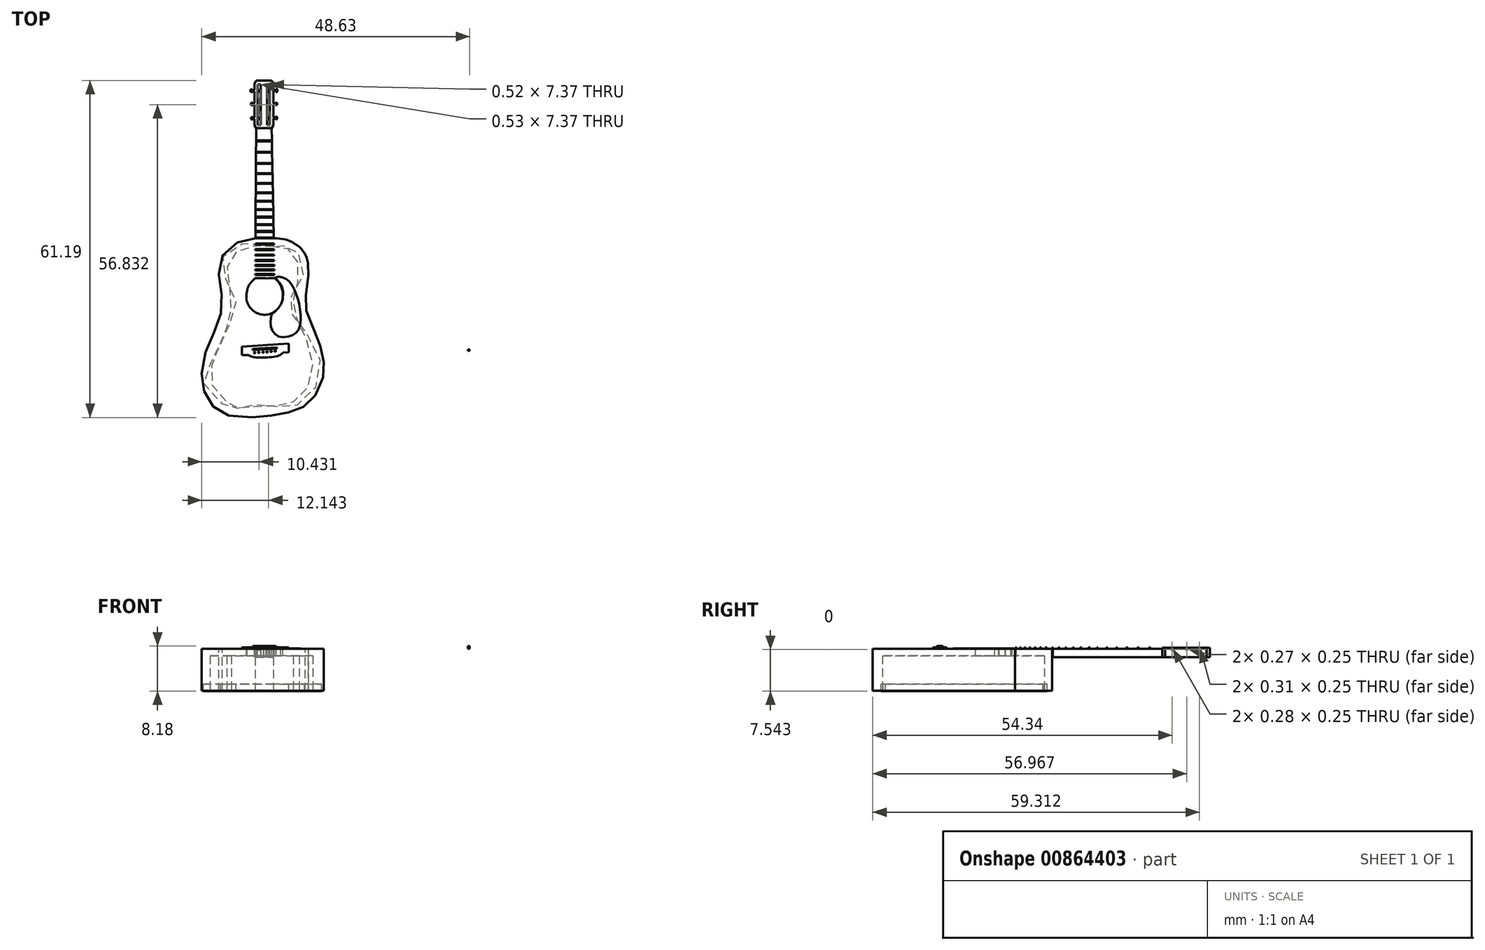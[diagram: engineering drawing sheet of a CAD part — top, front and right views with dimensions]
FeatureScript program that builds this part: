
annotation { "Feature Type Name" : "Feature", "Feature Type Description" : "" }
export const myFeature = defineFeature(function(context is Context, id is Id, definition is map)
    precondition{}
    {
        {
            var Q0;
            Q0=qCreatedBy(makeId("Top.planeOp"),FACE);
            var sketch = newSketch(context, id + "F0", { "sketchPlane" : qUnion([Q0])});
            skFitSpline(sketch, "E0", {"points": [v(22.3, 27.84) * mm, v(21.98, 25.02) * mm, v(21.82, 23.2) * mm, v(21.9, 21.62) * mm, v(22.91, 18.86) * mm, v(23.74, 17) * mm, v(24.5, 15.03) * mm, v(24.98, 13.15) * mm, v(25.13, 11.5) * mm, v(25.05, 9.87) * mm, v(24.78, 8.47) * mm, v(23.46, 5.83) * mm, v(22.27, 4.58) * mm, v(20.8, 3.57) * mm, v(19.22, 3.03) * mm, v(17.28, 2.58) * mm, v(15.34, 2.32) * mm, v(13.15, 2.13) * mm, v(9, 2.1) * mm, v(6.86, 2.83) * mm, v(5.05, 4) * mm, v(3.85, 5.8) * mm, v(3.1, 7.79) * mm, v(2.99, 9.87) * mm, v(3.35, 12.84) * mm, v(4.55, 16.01) * mm, v(5.6, 18.36) * mm, v(6.5, 21.1) * mm, v(6.69, 23.35) * mm, v(6.24, 26.4) * mm, v(6.08, 28.64) * mm, v(6.58, 31.1) * mm, v(8.32, 33.03) * mm, v(10.45, 34.2) * mm, v(12.74, 34.53) * mm], "startDerivative": vector(-10.71, -89.78) * mm, "endDerivative": vector(78.7, 5.6) * mm});
            skLineSegment(sketch, "E1", {"start": v(16.21, 27.29) * mm, "end": v(15.66, 54.52) * mm});
            skLineSegment(sketch, "E2", {"start": v(15.66, 54.52) * mm, "end": v(12.87, 54.52) * mm});
            skLineSegment(sketch, "E3", {"start": v(12.87, 54.52) * mm, "end": v(12.67, 27.29) * mm});
            skLineSegment(sketch, "E4", {"start": v(12.67, 27.29) * mm, "end": v(16.21, 27.29) * mm});
            skLineSegment(sketch, "E5", {"start": v(12.86, 52.31) * mm, "end": v(15.7, 52.37) * mm});
            skLineSegment(sketch, "E6", {"start": v(12.84, 50.24) * mm, "end": v(15.75, 50.3) * mm});
            skLineSegment(sketch, "E7", {"start": v(12.83, 48.25) * mm, "end": v(15.79, 48.22) * mm});
            skLineSegment(sketch, "E8", {"start": v(12.81, 46.37) * mm, "end": v(15.83, 46.35) * mm});
            skLineSegment(sketch, "E9", {"start": v(12.8, 44.6) * mm, "end": v(15.86, 44.58) * mm});
            skLineSegment(sketch, "E10", {"start": v(12.79, 42.9) * mm, "end": v(15.9, 42.87) * mm});
            skLineSegment(sketch, "E11", {"start": v(12.78, 41.39) * mm, "end": v(15.93, 41.36) * mm});
            skLineSegment(sketch, "E12", {"start": v(12.77, 39.85) * mm, "end": v(15.96, 39.83) * mm});
            skPoint(sketch, "E13.end.orphan", {"position": v(15.96, 38.48) * mm});
            skLineSegment(sketch, "E14", {"start": v(12.76, 38.46) * mm, "end": v(15.99, 38.46) * mm});
            skLineSegment(sketch, "E15", {"start": v(12.75, 37.12) * mm, "end": v(16.01, 37.12) * mm});
            skLineSegment(sketch, "E16", {"start": v(12.74, 35.86) * mm, "end": v(16.04, 35.86) * mm});
            skLineSegment(sketch, "E17", {"start": v(12.73, 34.67) * mm, "end": v(16.06, 34.67) * mm});
            skLineSegment(sketch, "E18", {"start": v(12.72, 33.58) * mm, "end": v(16.09, 33.58) * mm});
            skLineSegment(sketch, "E19", {"start": v(12.71, 32.56) * mm, "end": v(16.1, 32.56) * mm});
            skLineSegment(sketch, "E20", {"start": v(12.7, 31.58) * mm, "end": v(16.13, 31.58) * mm});
            skLineSegment(sketch, "E21", {"start": v(12.7, 30.6) * mm, "end": v(16.15, 30.6) * mm});
            skLineSegment(sketch, "E22", {"start": v(12.7, 29.73) * mm, "end": v(16.16, 29.73) * mm});
            skLineSegment(sketch, "E23", {"start": v(12.69, 28.89) * mm, "end": v(16.18, 28.89) * mm});
            skLineSegment(sketch, "E24", {"start": v(12.68, 28.04) * mm, "end": v(16.2, 28.04) * mm});
            skLineSegment(sketch, "E25", {"start": v(16.2, 28.04) * mm, "end": v(16.2, 28.06) * mm});
            skPoint(sketch, "E26.2.internal.orphan", {"position": v(15.85, 25.8) * mm});
            skPoint(sketch, "E27.0.internal.orphan", {"position": v(16.2, 34.53) * mm});
            skFitSpline(sketch, "E28", {"points": [v(22.3, 27.84) * mm, v(22.3, 28.93) * mm, v(22.2, 30.45) * mm, v(21.61, 31.9) * mm, v(20.8, 32.88) * mm, v(19.34, 33.86) * mm, v(17.95, 34.37) * mm, v(16.52, 34.55) * mm, v(16.07, 34.53) * mm], "startDerivative": vector(0, 9.07) * mm, "endDerivative": vector(-5.12, -0.57) * mm});
            skLineSegment(sketch, "E29", {"start": v(12.86, 52.31) * mm, "end": v(12.86, 52.14) * mm});
            skLineSegment(sketch, "E30", {"start": v(12.86, 52.14) * mm, "end": v(15.7, 52.12) * mm});
            skLineSegment(sketch, "E31", {"start": v(15.7, 52.12) * mm, "end": v(15.7, 52.37) * mm});
            skLineSegment(sketch, "E32", {"start": v(12.84, 50.24) * mm, "end": v(12.84, 50.06) * mm});
            skPoint(sketch, "E33.start.orphan", {"position": v(15.7, 50.12) * mm});
            skLineSegment(sketch, "E34", {"start": v(12.84, 50.06) * mm, "end": v(15.75, 50.12) * mm});
            skLineSegment(sketch, "E35", {"start": v(15.75, 50.12) * mm, "end": v(15.75, 50.3) * mm});
            skLineSegment(sketch, "E36", {"start": v(12.83, 48.25) * mm, "end": v(12.83, 48.06) * mm});
            skLineSegment(sketch, "E37", {"start": v(12.83, 48.06) * mm, "end": v(15.8, 48.04) * mm});
            skLineSegment(sketch, "E38", {"start": v(15.8, 48.04) * mm, "end": v(15.79, 48.22) * mm});
            skLineSegment(sketch, "E39", {"start": v(12.81, 46.37) * mm, "end": v(12.81, 46.2) * mm});
            skLineSegment(sketch, "E40", {"start": v(12.81, 46.2) * mm, "end": v(15.83, 46.18) * mm});
            skLineSegment(sketch, "E41", {"start": v(15.83, 46.18) * mm, "end": v(15.83, 46.35) * mm});
            skLineSegment(sketch, "E42", {"start": v(12.8, 44.6) * mm, "end": v(12.8, 44.42) * mm});
            skLineSegment(sketch, "E43", {"start": v(12.8, 44.42) * mm, "end": v(15.87, 44.4) * mm});
            skLineSegment(sketch, "E44", {"start": v(15.87, 44.4) * mm, "end": v(15.86, 44.58) * mm});
            skLineSegment(sketch, "E45", {"start": v(12.79, 42.9) * mm, "end": v(12.79, 42.71) * mm});
            skPoint(sketch, "E46.end.orphan", {"position": v(15.86, 42.69) * mm});
            skLineSegment(sketch, "E47", {"start": v(12.79, 42.71) * mm, "end": v(15.9, 42.69) * mm});
            skLineSegment(sketch, "E48", {"start": v(15.9, 42.69) * mm, "end": v(15.9, 42.87) * mm});
            skLineSegment(sketch, "E49", {"start": v(12.78, 41.39) * mm, "end": v(12.78, 41.2) * mm});
            skLineSegment(sketch, "E50", {"start": v(12.78, 41.2) * mm, "end": v(15.93, 41.18) * mm});
            skLineSegment(sketch, "E51", {"start": v(15.93, 41.18) * mm, "end": v(15.93, 41.36) * mm});
            skLineSegment(sketch, "E52", {"start": v(12.77, 39.85) * mm, "end": v(12.77, 39.67) * mm});
            skLineSegment(sketch, "E53", {"start": v(12.77, 39.67) * mm, "end": v(15.96, 39.65) * mm});
            skLineSegment(sketch, "E54", {"start": v(15.96, 39.65) * mm, "end": v(15.96, 39.83) * mm});
            skLineSegment(sketch, "E55", {"start": v(12.76, 38.46) * mm, "end": v(12.76, 38.3) * mm});
            skLineSegment(sketch, "E56", {"start": v(12.76, 38.3) * mm, "end": v(16, 38.3) * mm});
            skLineSegment(sketch, "E57", {"start": v(16, 38.3) * mm, "end": v(15.99, 38.46) * mm});
            skLineSegment(sketch, "E58", {"start": v(12.75, 37.12) * mm, "end": v(12.75, 36.93) * mm});
            skLineSegment(sketch, "E59", {"start": v(12.75, 36.93) * mm, "end": v(16.02, 36.93) * mm});
            skLineSegment(sketch, "E60", {"start": v(16.02, 36.93) * mm, "end": v(16.01, 37.12) * mm});
            skLineSegment(sketch, "E61", {"start": v(12.74, 35.86) * mm, "end": v(12.74, 35.69) * mm});
            skLineSegment(sketch, "E62", {"start": v(12.74, 35.69) * mm, "end": v(16.04, 35.69) * mm});
            skLineSegment(sketch, "E63", {"start": v(16.04, 35.69) * mm, "end": v(16.04, 35.86) * mm});
            skLineSegment(sketch, "E64", {"start": v(12.73, 34.67) * mm, "end": v(12.74, 34.53) * mm});
            skLineSegment(sketch, "E65", {"start": v(12.74, 34.53) * mm, "end": v(16.07, 34.53) * mm});
            skLineSegment(sketch, "E66", {"start": v(16.07, 34.53) * mm, "end": v(16.06, 34.67) * mm});
            skLineSegment(sketch, "E67", {"start": v(12.72, 33.58) * mm, "end": v(12.72, 33.4) * mm});
            skPoint(sketch, "E68.end.orphan", {"position": v(16.06, 33.37) * mm});
            skLineSegment(sketch, "E69", {"start": v(12.72, 33.4) * mm, "end": v(16.1, 33.37) * mm});
            skLineSegment(sketch, "E70", {"start": v(16.1, 33.37) * mm, "end": v(16.09, 33.58) * mm});
            skLineSegment(sketch, "E71", {"start": v(12.71, 32.56) * mm, "end": v(12.71, 32.38) * mm});
            skPoint(sketch, "E72.end.orphan", {"position": v(16.09, 32.36) * mm});
            skLineSegment(sketch, "E73", {"start": v(12.71, 32.38) * mm, "end": v(16.11, 32.36) * mm});
            skLineSegment(sketch, "E74", {"start": v(16.11, 32.36) * mm, "end": v(16.1, 32.56) * mm});
            skLineSegment(sketch, "E75", {"start": v(12.7, 31.58) * mm, "end": v(12.7, 31.4) * mm});
            skLineSegment(sketch, "E76", {"start": v(12.7, 31.4) * mm, "end": v(16.13, 31.38) * mm});
            skLineSegment(sketch, "E77", {"start": v(16.13, 31.38) * mm, "end": v(16.13, 31.58) * mm});
            skLineSegment(sketch, "E78", {"start": v(12.7, 30.6) * mm, "end": v(12.7, 30.41) * mm});
            skLineSegment(sketch, "E79", {"start": v(12.7, 30.41) * mm, "end": v(16.13, 30.41) * mm});
            skLineSegment(sketch, "E80", {"start": v(16.13, 30.41) * mm, "end": v(16.15, 30.6) * mm});
            skLineSegment(sketch, "E81", {"start": v(12.7, 29.73) * mm, "end": v(12.7, 29.56) * mm});
            skLineSegment(sketch, "E82", {"start": v(12.7, 29.56) * mm, "end": v(16.17, 29.53) * mm});
            skLineSegment(sketch, "E83", {"start": v(16.17, 29.53) * mm, "end": v(16.16, 29.73) * mm});
            skLineSegment(sketch, "E84", {"start": v(12.69, 28.89) * mm, "end": v(12.69, 28.72) * mm});
            skLineSegment(sketch, "E85", {"start": v(12.69, 28.72) * mm, "end": v(16.17, 28.7) * mm});
            skLineSegment(sketch, "E86", {"start": v(16.17, 28.7) * mm, "end": v(16.18, 28.89) * mm});
            skLineSegment(sketch, "E87", {"start": v(12.68, 28.04) * mm, "end": v(12.68, 27.88) * mm});
            skLineSegment(sketch, "E88", {"start": v(12.68, 27.88) * mm, "end": v(16.2, 27.88) * mm});
            skLineSegment(sketch, "E89", {"start": v(16.2, 27.88) * mm, "end": v(16.2, 28.06) * mm});
            skLineSegment(sketch, "E90", {"start": v(12.87, 54.52) * mm, "end": v(12.53, 55.04) * mm});
            skLineSegment(sketch, "E91", {"start": v(12.53, 55.04) * mm, "end": v(12.53, 62.64) * mm});
            skLineSegment(sketch, "E92", {"start": v(12.53, 62.64) * mm, "end": v(12.87, 63.19) * mm});
            skLineSegment(sketch, "E93", {"start": v(12.87, 63.19) * mm, "end": v(14, 63.18) * mm});
            skPoint(sketch, "E94.startSnap0", {"position": v(12.7, 62.91) * mm});
            skPoint(sketch, "E94.startSnap1", {"position": v(13.44, 63.18) * mm});
            skLineSegment(sketch, "E95", {"start": v(14, 63.18) * mm, "end": v(14.27, 63.18) * mm});
            skLineSegment(sketch, "E96", {"start": v(14.27, 54.52) * mm, "end": v(14.27, 63.18) * mm, "construction": true});
            skPoint(sketch, "E94.start.orphan", {"position": v(13.44, 62.91) * mm});
            skLineSegment(sketch, "E97.bottom", {"start": v(13.15, 62.52) * mm, "end": v(13.67, 62.52) * mm});
            skLineSegment(sketch, "E97.top", {"start": v(13.15, 55.15) * mm, "end": v(13.67, 55.15) * mm});
            skLineSegment(sketch, "E97.left", {"start": v(13.15, 62.52) * mm, "end": v(13.15, 56.61) * mm});
            skLineSegment(sketch, "E97.right", {"start": v(13.67, 62.52) * mm, "end": v(13.67, 55.15) * mm});
            skLineSegment(sketch, "E98", {"start": v(13.15, 61.47) * mm, "end": v(13.67, 61.47) * mm});
            skLineSegment(sketch, "E99", {"start": v(13.67, 61.47) * mm, "end": v(13.67, 61.16) * mm});
            skLineSegment(sketch, "E100", {"start": v(13.67, 61.16) * mm, "end": v(13.15, 61.16) * mm});
            skLineSegment(sketch, "E101", {"start": v(13.15, 61.16) * mm, "end": v(13.15, 61.47) * mm});
            skPoint(sketch, "E102.start.orphan", {"position": v(13.15, 59.64) * mm});
            skPoint(sketch, "E103.end.orphan", {"position": v(13.15, 56.92) * mm});
            skLineSegment(sketch, "E104", {"start": v(13.15, 56.2) * mm, "end": v(13.67, 56.2) * mm});
            skLineSegment(sketch, "E105", {"start": v(13.15, 58.83) * mm, "end": v(13.67, 58.83) * mm});
            skLineSegment(sketch, "E106", {"start": v(13.67, 58.83) * mm, "end": v(13.67, 59.1) * mm});
            skLineSegment(sketch, "E107", {"start": v(13.67, 59.1) * mm, "end": v(13.15, 59.1) * mm});
            skLineSegment(sketch, "E108", {"start": v(13.15, 59.1) * mm, "end": v(13.15, 58.83) * mm});
            skLineSegment(sketch, "E109.trimOffspring", {"start": v(13.15, 56.2) * mm, "end": v(13.15, 55.15) * mm});
            skLineSegment(sketch, "E110", {"start": v(13.15, 56.61) * mm, "end": v(13.15, 56.2) * mm});
            skPoint(sketch, "E111.startSnap0", {"position": v(13.15, 56.4) * mm});
            skLineSegment(sketch, "E112", {"start": v(13.15, 56.2) * mm, "end": v(13.15, 56.48) * mm});
            skLineSegment(sketch, "E113", {"start": v(13.15, 56.48) * mm, "end": v(13.67, 56.48) * mm});
            skLineSegment(sketch, "E114", {"start": v(13.67, 56.48) * mm, "end": v(13.67, 56.2) * mm});
            skLineSegment(sketch, "E115.MirrorCS", {"start": v(15.66, 63.19) * mm, "end": v(14.53, 63.18) * mm});
            skLineSegment(sketch, "E116.MirrorCS", {"start": v(14.53, 63.18) * mm, "end": v(14.27, 63.18) * mm});
            skLineSegment(sketch, "E117.MirrorCS", {"start": v(16, 62.64) * mm, "end": v(15.66, 63.19) * mm});
            skLineSegment(sketch, "E118.MirrorCS", {"start": v(16, 55.04) * mm, "end": v(16, 62.64) * mm});
            skLineSegment(sketch, "E119.MirrorCS", {"start": v(15.39, 62.52) * mm, "end": v(14.86, 62.52) * mm});
            skLineSegment(sketch, "E120.MirrorCS", {"start": v(14.86, 62.52) * mm, "end": v(14.86, 55.15) * mm});
            skLineSegment(sketch, "E121.MirrorCS", {"start": v(15.39, 62.52) * mm, "end": v(15.39, 56.61) * mm});
            skLineSegment(sketch, "E122.MirrorCS", {"start": v(15.39, 61.47) * mm, "end": v(14.86, 61.47) * mm});
            skLineSegment(sketch, "E123.MirrorCS", {"start": v(14.86, 61.16) * mm, "end": v(15.39, 61.16) * mm});
            skLineSegment(sketch, "E124.MirrorCS", {"start": v(14.86, 59.1) * mm, "end": v(15.39, 59.1) * mm});
            skLineSegment(sketch, "E125.MirrorCS", {"start": v(15.39, 58.83) * mm, "end": v(14.86, 58.83) * mm});
            skLineSegment(sketch, "E126.MirrorCS", {"start": v(15.66, 54.52) * mm, "end": v(16, 55.04) * mm});
            skLineSegment(sketch, "E127.MirrorCS", {"start": v(15.39, 55.15) * mm, "end": v(14.86, 55.15) * mm});
            skLineSegment(sketch, "E128.MirrorCS", {"start": v(15.39, 56.2) * mm, "end": v(14.86, 56.2) * mm});
            skLineSegment(sketch, "E129.MirrorCS", {"start": v(15.39, 56.48) * mm, "end": v(14.86, 56.48) * mm});
            skLineSegment(sketch, "E130.MirrorCS", {"start": v(14.86, 56.48) * mm, "end": v(14.86, 56.2) * mm});
            skLineSegment(sketch, "E131.MirrorCS", {"start": v(15.39, 56.2) * mm, "end": v(15.39, 56.48) * mm});
            skLineSegment(sketch, "E132.MirrorCS", {"start": v(15.39, 56.61) * mm, "end": v(15.39, 56.2) * mm});
            skLineSegment(sketch, "E133.MirrorCS", {"start": v(15.39, 56.2) * mm, "end": v(15.39, 55.15) * mm});
            skSolve(sketch);
        }
        {
            var Q0;
            Q0=makeQuery(id+"F0.imprint","IMPRINT",FACE,{"disambiguationData":[TD([[makeQuery(id+"F0.imprint","IMPRINT",EDGE,{"derivedFrom":sQuery(id+"F0.wireOp",EDGE,"E2")}),-1.0]])]});
            extrude(context, id + "F1", {"entities" : qUnion([Q0]), "oppositeDirection" : true, "depth" : 1.52 * mm, "offsetDistance" : 25.4 * mm});
        }
        {
            var Q0;
            Q0=makeQuery(id+"F0.imprint","IMPRINT",FACE,{"disambiguationData":[TD([[makeQuery(id+"F0.imprint","IMPRINT",EDGE,{"derivedFrom":sQuery(id+"F0.wireOp",EDGE,"E2")}),-1.0]])]});
            extrude(context, id + "F2", {"entities" : qUnion([Q0]), "operationType" : NewBodyOperationType.ADD, "depth" : 0.2 * mm, "offsetDistance" : 25.4 * mm});
        }
        {
            var Q0;
            {var subQ15=sQuery(id+"F0.wireOp",EDGE,"E4");Q0=makeQuery(id+"F0.imprint","IMPRINT",FACE,{"disambiguationData":[TD([[makeQuery(id+"F0.imprint","IMPRINT",EDGE,{"derivedFrom":subQ15}),-1.0]])]});}
            var sketch = newSketch(context, id + "F3", { "sketchPlane" : qUnion([Q0])});
            skLineSegment(sketch, "E134", {"start": v(10.28, 14.9) * mm, "end": v(18.78, 15.4) * mm});
            skLineSegment(sketch, "E135", {"start": v(18.78, 15.4) * mm, "end": v(18.78, 13.85) * mm});
            skLineSegment(sketch, "E136", {"start": v(10.28, 14.9) * mm, "end": v(10.28, 13.34) * mm});
            skLineSegment(sketch, "E137", {"start": v(10.28, 13.34) * mm, "end": v(11.4, 13.34) * mm});
            skLineSegment(sketch, "E138", {"start": v(18.78, 13.85) * mm, "end": v(17.72, 13.79) * mm});
            skFitSpline(sketch, "E139", {"points": [v(11.4, 13.34) * mm, v(12.33, 12.98) * mm, v(16.77, 13.2) * mm, v(17.72, 13.79) * mm], "startDerivative": vector(2.7, -1.74) * mm, "endDerivative": vector(2.46, 2.6) * mm});
            skSolve(sketch);
        }
        {
            var Q0;
            {var subQ15=sQuery(id+"F0.wireOp",EDGE,"E4");Q0=makeQuery(id+"F0.imprint","IMPRINT",FACE,{"disambiguationData":[TD([[makeQuery(id+"F0.imprint","IMPRINT",EDGE,{"derivedFrom":subQ15}),-1.0]])]});}
            var sketch = newSketch(context, id + "F4", { "sketchPlane" : qUnion([Q0])});
            skLineSegment(sketch, "E140", {"start": v(12.22, 14.2) * mm, "end": v(12.22, 14.45) * mm});
            skLineSegment(sketch, "E141", {"start": v(16.63, 14.74) * mm, "end": v(12.22, 14.45) * mm});
            skLineSegment(sketch, "E142", {"start": v(12.22, 14.2) * mm, "end": v(16.65, 14.49) * mm});
            skLineSegment(sketch, "E143", {"start": v(16.65, 14.49) * mm, "end": v(16.63, 14.74) * mm});
            skCircle(sketch, "E144.2.0.0", {"center": v(51.47, 14.23) * mm, "radius": 0.15 * mm});
            skPoint(sketch, "E145.end.orphan", {"position": v(13.36, 12.9) * mm});
            skPoint(sketch, "E146.end.orphan", {"position": v(15.65, 13) * mm});
            skPoint(sketch, "E147.orphan", {"position": v(14.43, 14.6) * mm});
            skCircle(sketch, "E148", {"center": v(12.58, 13.78) * mm, "radius": 0.12 * mm});
            skCircle(sketch, "E149", {"center": v(13.35, 13.83) * mm, "radius": 0.12 * mm});
            skCircle(sketch, "E150", {"center": v(14.12, 13.87) * mm, "radius": 0.12 * mm});
            skCircle(sketch, "E151", {"center": v(14.83, 13.93) * mm, "radius": 0.12 * mm});
            skCircle(sketch, "E152", {"center": v(15.58, 14) * mm, "radius": 0.12 * mm});
            skCircle(sketch, "E153", {"center": v(16.32, 14.07) * mm, "radius": 0.12 * mm});
            skPoint(sketch, "E154.end.orphan", {"position": v(12.36, 13) * mm});
            skPoint(sketch, "E155.end.orphan", {"position": v(13.03, 12.9) * mm});
            skPoint(sketch, "E156.start.orphan", {"position": v(13.84, 12.9) * mm});
            skSolve(sketch);
        }
        {
            var Q0;
            {var subQ0=sQuery(id+"F0.wireOp",EDGE,"E24");Q0=makeQuery(id+"F0.imprint","IMPRINT",FACE,{"disambiguationData":[TD([[makeQuery(id+"F0.imprint","IMPRINT",EDGE,{"derivedFrom":subQ0}),-1.0]])]});}
            var Q1;
            Q1=makeQuery(id+"F0.imprint","IMPRINT",FACE,{"disambiguationData":[TD([[makeQuery(id+"F0.imprint","IMPRINT",EDGE,{"derivedFrom":sQuery(id+"F0.wireOp",EDGE,"E23")}),-1.0]])]});
            var Q2;
            Q2=makeQuery(id+"F0.imprint","IMPRINT",FACE,{"disambiguationData":[TD([[makeQuery(id+"F0.imprint","IMPRINT",EDGE,{"derivedFrom":sQuery(id+"F0.wireOp",EDGE,"E22")}),-1.0]])]});
            var Q3;
            Q3=makeQuery(id+"F0.imprint","IMPRINT",FACE,{"disambiguationData":[TD([[makeQuery(id+"F0.imprint","IMPRINT",EDGE,{"derivedFrom":sQuery(id+"F0.wireOp",EDGE,"E21")}),-1.0]])]});
            var Q4;
            Q4=makeQuery(id+"F0.imprint","IMPRINT",FACE,{"disambiguationData":[TD([[makeQuery(id+"F0.imprint","IMPRINT",EDGE,{"derivedFrom":sQuery(id+"F0.wireOp",EDGE,"E20")}),-1.0]])]});
            var Q5;
            Q5=makeQuery(id+"F0.imprint","IMPRINT",FACE,{"disambiguationData":[TD([[makeQuery(id+"F0.imprint","IMPRINT",EDGE,{"derivedFrom":sQuery(id+"F0.wireOp",EDGE,"E19")}),-1.0]])]});
            var Q6;
            Q6=makeQuery(id+"F0.imprint","IMPRINT",FACE,{"disambiguationData":[TD([[makeQuery(id+"F0.imprint","IMPRINT",EDGE,{"derivedFrom":sQuery(id+"F0.wireOp",EDGE,"E18")}),-1.0]])]});
            var Q7;
            Q7=makeQuery(id+"F0.imprint","IMPRINT",FACE,{"disambiguationData":[TD([[makeQuery(id+"F0.imprint","IMPRINT",EDGE,{"derivedFrom":sQuery(id+"F0.wireOp",EDGE,"E17")}),-1.0]])]});
            var Q8;
            Q8=makeQuery(id+"F0.imprint","IMPRINT",FACE,{"disambiguationData":[TD([[makeQuery(id+"F0.imprint","IMPRINT",EDGE,{"derivedFrom":sQuery(id+"F0.wireOp",EDGE,"E16")}),-1.0]])]});
            var Q9;
            Q9=makeQuery(id+"F0.imprint","IMPRINT",FACE,{"disambiguationData":[TD([[makeQuery(id+"F0.imprint","IMPRINT",EDGE,{"derivedFrom":sQuery(id+"F0.wireOp",EDGE,"E15")}),-1.0]])]});
            var Q10;
            Q10=makeQuery(id+"F0.imprint","IMPRINT",FACE,{"disambiguationData":[TD([[makeQuery(id+"F0.imprint","IMPRINT",EDGE,{"derivedFrom":sQuery(id+"F0.wireOp",EDGE,"E14")}),-1.0]])]});
            var Q11;
            Q11=makeQuery(id+"F0.imprint","IMPRINT",FACE,{"disambiguationData":[TD([[makeQuery(id+"F0.imprint","IMPRINT",EDGE,{"derivedFrom":sQuery(id+"F0.wireOp",EDGE,"E12")}),-1.0]])]});
            var Q12;
            Q12=makeQuery(id+"F0.imprint","IMPRINT",FACE,{"disambiguationData":[TD([[makeQuery(id+"F0.imprint","IMPRINT",EDGE,{"derivedFrom":sQuery(id+"F0.wireOp",EDGE,"E11")}),-1.0]])]});
            var Q13;
            Q13=makeQuery(id+"F0.imprint","IMPRINT",FACE,{"disambiguationData":[TD([[makeQuery(id+"F0.imprint","IMPRINT",EDGE,{"derivedFrom":sQuery(id+"F0.wireOp",EDGE,"E10")}),-1.0]])]});
            var Q14;
            Q14=makeQuery(id+"F0.imprint","IMPRINT",FACE,{"disambiguationData":[TD([[makeQuery(id+"F0.imprint","IMPRINT",EDGE,{"derivedFrom":sQuery(id+"F0.wireOp",EDGE,"E9")}),-1.0]])]});
            var Q15;
            Q15=makeQuery(id+"F0.imprint","IMPRINT",FACE,{"disambiguationData":[TD([[makeQuery(id+"F0.imprint","IMPRINT",EDGE,{"derivedFrom":sQuery(id+"F0.wireOp",EDGE,"E8")}),-1.0]])]});
            var Q16;
            Q16=makeQuery(id+"F0.imprint","IMPRINT",FACE,{"disambiguationData":[TD([[makeQuery(id+"F0.imprint","IMPRINT",EDGE,{"derivedFrom":sQuery(id+"F0.wireOp",EDGE,"E7")}),-1.0]])]});
            var Q17;
            Q17=makeQuery(id+"F0.imprint","IMPRINT",FACE,{"disambiguationData":[TD([[makeQuery(id+"F0.imprint","IMPRINT",EDGE,{"derivedFrom":sQuery(id+"F0.wireOp",EDGE,"E6")}),-1.0]])]});
            var Q18;
            Q18=makeQuery(id+"F0.imprint","IMPRINT",FACE,{"disambiguationData":[TD([[makeQuery(id+"F0.imprint","IMPRINT",EDGE,{"derivedFrom":sQuery(id+"F0.wireOp",EDGE,"E5")}),-1.0]])]});
            extrude(context, id + "F5", {"entities" : qUnion([Q0, Q1, Q2, Q3, Q4, Q5, Q6, Q7, Q8, Q9, Q10, Q11, Q12, Q13, Q14, Q15, Q16, Q17, Q18]), "depth" : 0.25 * mm, "offsetDistance" : 25.4 * mm});
        }
        {
            var Q0;
            {var subQ2=sQuery(id+"F0.wireOp",EDGE,"E4");Q0=makeQuery(id+"F0.imprint","IMPRINT",FACE,{"disambiguationData":[TD([[makeQuery(id+"F0.imprint","IMPRINT",EDGE,{"derivedFrom":subQ2}),-1.0]])]});}
            var Q1;
            {var subQ0=sQuery(id+"F0.wireOp",EDGE,"E20");Q1=makeQuery(id+"F0.imprint","IMPRINT",FACE,{"disambiguationData":[TD([[makeQuery(id+"F0.imprint","IMPRINT",EDGE,{"derivedFrom":subQ0}),1.0]])]});}
            var Q2;
            {var subQ0=sQuery(id+"F0.wireOp",EDGE,"E21");Q2=makeQuery(id+"F0.imprint","IMPRINT",FACE,{"disambiguationData":[TD([[makeQuery(id+"F0.imprint","IMPRINT",EDGE,{"derivedFrom":subQ0}),1.0]])]});}
            var Q3;
            {var subQ1=sQuery(id+"F0.wireOp",EDGE,"E22");Q3=makeQuery(id+"F0.imprint","IMPRINT",FACE,{"disambiguationData":[TD([[makeQuery(id+"F0.imprint","IMPRINT",EDGE,{"derivedFrom":subQ1}),1.0]])]});}
            var Q4;
            {var subQ0=sQuery(id+"F0.wireOp",EDGE,"E23");Q4=makeQuery(id+"F0.imprint","IMPRINT",FACE,{"disambiguationData":[TD([[makeQuery(id+"F0.imprint","IMPRINT",EDGE,{"derivedFrom":subQ0}),1.0]])]});}
            var Q5;
            {var subQ1=sQuery(id+"F0.wireOp",EDGE,"E24");Q5=makeQuery(id+"F0.imprint","IMPRINT",FACE,{"disambiguationData":[TD([[makeQuery(id+"F0.imprint","IMPRINT",EDGE,{"derivedFrom":subQ1}),1.0]])]});}
            var Q6;
            {var subQ0=sQuery(id+"F0.wireOp",EDGE,"E4");Q6=makeQuery(id+"F0.imprint","IMPRINT",FACE,{"disambiguationData":[TD([[makeQuery(id+"F0.imprint","IMPRINT",EDGE,{"derivedFrom":subQ0}),1.0]])]});}
            var Q7;
            {var subQ0=sQuery(id+"F0.wireOp",EDGE,"E18");Q7=makeQuery(id+"F0.imprint","IMPRINT",FACE,{"disambiguationData":[TD([[makeQuery(id+"F0.imprint","IMPRINT",EDGE,{"derivedFrom":subQ0}),1.0]])]});}
            var Q8;
            {var subQ0=sQuery(id+"F0.wireOp",EDGE,"E19");Q8=makeQuery(id+"F0.imprint","IMPRINT",FACE,{"disambiguationData":[TD([[makeQuery(id+"F0.imprint","IMPRINT",EDGE,{"derivedFrom":subQ0}),1.0]])]});}
            var Q9;
            Q9=makeQuery(id+"F0.imprint","IMPRINT",FACE,{"disambiguationData":[TD([[makeQuery(id+"F0.imprint","IMPRINT",EDGE,{"derivedFrom":sQuery(id+"F0.wireOp",EDGE,"E19")}),-1.0]])]});
            var Q10;
            Q10=makeQuery(id+"F0.imprint","IMPRINT",FACE,{"disambiguationData":[TD([[makeQuery(id+"F0.imprint","IMPRINT",EDGE,{"derivedFrom":sQuery(id+"F0.wireOp",EDGE,"E18")}),-1.0]])]});
            var Q11;
            Q11=makeQuery(id+"F0.imprint","IMPRINT",FACE,{"disambiguationData":[TD([[makeQuery(id+"F0.imprint","IMPRINT",EDGE,{"derivedFrom":sQuery(id+"F0.wireOp",EDGE,"E20")}),-1.0]])]});
            var Q12;
            Q12=makeQuery(id+"F0.imprint","IMPRINT",FACE,{"disambiguationData":[TD([[makeQuery(id+"F0.imprint","IMPRINT",EDGE,{"derivedFrom":sQuery(id+"F0.wireOp",EDGE,"E21")}),-1.0]])]});
            var Q13;
            Q13=makeQuery(id+"F0.imprint","IMPRINT",FACE,{"disambiguationData":[TD([[makeQuery(id+"F0.imprint","IMPRINT",EDGE,{"derivedFrom":sQuery(id+"F0.wireOp",EDGE,"E23")}),-1.0]])]});
            var Q14;
            {var subQ0=sQuery(id+"F0.wireOp",EDGE,"E24");Q14=makeQuery(id+"F0.imprint","IMPRINT",FACE,{"disambiguationData":[TD([[makeQuery(id+"F0.imprint","IMPRINT",EDGE,{"derivedFrom":subQ0}),-1.0]])]});}
            var Q15;
            Q15=makeQuery(id+"F0.imprint","IMPRINT",FACE,{"disambiguationData":[TD([[makeQuery(id+"F0.imprint","IMPRINT",EDGE,{"derivedFrom":sQuery(id+"F0.wireOp",EDGE,"E22")}),-1.0]])]});
            extrude(context, id + "F6", {"entities" : qUnion([Q0, Q1, Q2, Q3, Q4, Q5, Q6, Q7, Q8, Q9, Q10, Q11, Q12, Q13, Q14, Q15]), "oppositeDirection" : true, "depth" : 7.62 * mm, "offsetDistance" : 25.4 * mm});
        }
        {
            var Q0;
            Q0=makeQuery(id+"F6.opExtrude","CAP_FACE",FACE,{"disambiguationData":[OSD([sQuery(id+"F0.wireOp",EDGE,"E0"),sQuery(id+"F0.wireOp",EDGE,"E1"),sQuery(id+"F0.wireOp",EDGE,"E25"),sQuery(id+"F0.wireOp",EDGE,"E28"),sQuery(id+"F0.wireOp",EDGE,"E65"),sQuery(id+"F0.wireOp",EDGE,"E89")])],"isStart":false});
            var sketch = newSketch(context, id + "F7", { "sketchPlane" : qUnion([Q0])});
            skFitSpline(sketch, "E157", {"points": [v(16, -33) * mm, v(11.02, -32.92) * mm, v(7.67, -29.88) * mm, v(8.35, -23.6) * mm, v(7.23, -17.65) * mm, v(5.33, -12.93) * mm, v(4.87, -7.9) * mm, v(9, -3.82) * mm, v(9.82, -3.83) * mm, v(15.51, -4.12) * mm, v(19.93, -5) * mm, v(23.15, -10.26) * mm, v(20.83, -18.8) * mm, v(19.6, -23.11) * mm, v(20.69, -28.64) * mm, v(18.87, -32.47) * mm, v(16, -33) * mm]});
            skSolve(sketch);
        }
        {
            var Q0;
            Q0=makeQuery(id+"F7.imprint","IMPRINT",FACE,{"disambiguationData":[TD([[makeQuery(id+"F7.imprint","IMPRINT",EDGE,{"derivedFrom":sQuery(id+"F7.wireOp",EDGE,"E157")}),-1.0]])]});
            extrude(context, id + "F8", {"entities" : qUnion([Q0]), "operationType" : NewBodyOperationType.REMOVE, "oppositeDirection" : true, "depth" : 6.35 * mm, "offsetDistance" : 25.4 * mm});
        }
        {
            var Q0;
            {var subQ0=sQuery(id+"F0.wireOp",EDGE,"E17");Q0=makeQuery(id+"F0.imprint","IMPRINT",FACE,{"disambiguationData":[TD([[makeQuery(id+"F0.imprint","IMPRINT",EDGE,{"derivedFrom":subQ0}),1.0]])]});}
            var Q1;
            {var subQ0=sQuery(id+"F0.wireOp",EDGE,"E16");Q1=makeQuery(id+"F0.imprint","IMPRINT",FACE,{"disambiguationData":[TD([[makeQuery(id+"F0.imprint","IMPRINT",EDGE,{"derivedFrom":subQ0}),1.0]])]});}
            var Q2;
            {var subQ0=sQuery(id+"F0.wireOp",EDGE,"E15");Q2=makeQuery(id+"F0.imprint","IMPRINT",FACE,{"disambiguationData":[TD([[makeQuery(id+"F0.imprint","IMPRINT",EDGE,{"derivedFrom":subQ0}),1.0]])]});}
            var Q3;
            {var subQ0=sQuery(id+"F0.wireOp",EDGE,"E14");Q3=makeQuery(id+"F0.imprint","IMPRINT",FACE,{"disambiguationData":[TD([[makeQuery(id+"F0.imprint","IMPRINT",EDGE,{"derivedFrom":subQ0}),1.0]])]});}
            var Q4;
            {var subQ0=sQuery(id+"F0.wireOp",EDGE,"E12");Q4=makeQuery(id+"F0.imprint","IMPRINT",FACE,{"disambiguationData":[TD([[makeQuery(id+"F0.imprint","IMPRINT",EDGE,{"derivedFrom":subQ0}),1.0]])]});}
            var Q5;
            {var subQ0=sQuery(id+"F0.wireOp",EDGE,"E11");Q5=makeQuery(id+"F0.imprint","IMPRINT",FACE,{"disambiguationData":[TD([[makeQuery(id+"F0.imprint","IMPRINT",EDGE,{"derivedFrom":subQ0}),1.0]])]});}
            var Q6;
            {var subQ0=sQuery(id+"F0.wireOp",EDGE,"E10");Q6=makeQuery(id+"F0.imprint","IMPRINT",FACE,{"disambiguationData":[TD([[makeQuery(id+"F0.imprint","IMPRINT",EDGE,{"derivedFrom":subQ0}),1.0]])]});}
            var Q7;
            {var subQ0=sQuery(id+"F0.wireOp",EDGE,"E9");Q7=makeQuery(id+"F0.imprint","IMPRINT",FACE,{"disambiguationData":[TD([[makeQuery(id+"F0.imprint","IMPRINT",EDGE,{"derivedFrom":subQ0}),1.0]])]});}
            var Q8;
            {var subQ0=sQuery(id+"F0.wireOp",EDGE,"E8");Q8=makeQuery(id+"F0.imprint","IMPRINT",FACE,{"disambiguationData":[TD([[makeQuery(id+"F0.imprint","IMPRINT",EDGE,{"derivedFrom":subQ0}),1.0]])]});}
            var Q9;
            {var subQ0=sQuery(id+"F0.wireOp",EDGE,"E7");Q9=makeQuery(id+"F0.imprint","IMPRINT",FACE,{"disambiguationData":[TD([[makeQuery(id+"F0.imprint","IMPRINT",EDGE,{"derivedFrom":subQ0}),1.0]])]});}
            var Q10;
            {var subQ0=sQuery(id+"F0.wireOp",EDGE,"E6");Q10=makeQuery(id+"F0.imprint","IMPRINT",FACE,{"disambiguationData":[TD([[makeQuery(id+"F0.imprint","IMPRINT",EDGE,{"derivedFrom":subQ0}),1.0]])]});}
            var Q11;
            {var subQ0=sQuery(id+"F0.wireOp",EDGE,"E2");Q11=makeQuery(id+"F0.imprint","IMPRINT",FACE,{"disambiguationData":[TD([[makeQuery(id+"F0.imprint","IMPRINT",EDGE,{"derivedFrom":subQ0}),1.0]])]});}
            var Q12;
            Q12=makeQuery(id+"F0.imprint","IMPRINT",FACE,{"disambiguationData":[TD([[makeQuery(id+"F0.imprint","IMPRINT",EDGE,{"derivedFrom":sQuery(id+"F0.wireOp",EDGE,"E5")}),-1.0]])]});
            var Q13;
            Q13=makeQuery(id+"F0.imprint","IMPRINT",FACE,{"disambiguationData":[TD([[makeQuery(id+"F0.imprint","IMPRINT",EDGE,{"derivedFrom":sQuery(id+"F0.wireOp",EDGE,"E6")}),-1.0]])]});
            var Q14;
            Q14=makeQuery(id+"F0.imprint","IMPRINT",FACE,{"disambiguationData":[TD([[makeQuery(id+"F0.imprint","IMPRINT",EDGE,{"derivedFrom":sQuery(id+"F0.wireOp",EDGE,"E7")}),-1.0]])]});
            var Q15;
            Q15=makeQuery(id+"F0.imprint","IMPRINT",FACE,{"disambiguationData":[TD([[makeQuery(id+"F0.imprint","IMPRINT",EDGE,{"derivedFrom":sQuery(id+"F0.wireOp",EDGE,"E8")}),-1.0]])]});
            var Q16;
            Q16=makeQuery(id+"F0.imprint","IMPRINT",FACE,{"disambiguationData":[TD([[makeQuery(id+"F0.imprint","IMPRINT",EDGE,{"derivedFrom":sQuery(id+"F0.wireOp",EDGE,"E10")}),-1.0]])]});
            var Q17;
            Q17=makeQuery(id+"F0.imprint","IMPRINT",FACE,{"disambiguationData":[TD([[makeQuery(id+"F0.imprint","IMPRINT",EDGE,{"derivedFrom":sQuery(id+"F0.wireOp",EDGE,"E9")}),-1.0]])]});
            var Q18;
            Q18=makeQuery(id+"F0.imprint","IMPRINT",FACE,{"disambiguationData":[TD([[makeQuery(id+"F0.imprint","IMPRINT",EDGE,{"derivedFrom":sQuery(id+"F0.wireOp",EDGE,"E11")}),-1.0]])]});
            var Q19;
            Q19=makeQuery(id+"F0.imprint","IMPRINT",FACE,{"disambiguationData":[TD([[makeQuery(id+"F0.imprint","IMPRINT",EDGE,{"derivedFrom":sQuery(id+"F0.wireOp",EDGE,"E12")}),-1.0]])]});
            var Q20;
            Q20=makeQuery(id+"F0.imprint","IMPRINT",FACE,{"disambiguationData":[TD([[makeQuery(id+"F0.imprint","IMPRINT",EDGE,{"derivedFrom":sQuery(id+"F0.wireOp",EDGE,"E15")}),-1.0]])]});
            var Q21;
            Q21=makeQuery(id+"F0.imprint","IMPRINT",FACE,{"disambiguationData":[TD([[makeQuery(id+"F0.imprint","IMPRINT",EDGE,{"derivedFrom":sQuery(id+"F0.wireOp",EDGE,"E16")}),-1.0]])]});
            var Q22;
            Q22=makeQuery(id+"F0.imprint","IMPRINT",FACE,{"disambiguationData":[TD([[makeQuery(id+"F0.imprint","IMPRINT",EDGE,{"derivedFrom":sQuery(id+"F0.wireOp",EDGE,"E14")}),-1.0]])]});
            extrude(context, id + "F9", {"entities" : qUnion([Q0, Q1, Q2, Q3, Q4, Q5, Q6, Q7, Q8, Q9, Q10, Q11, Q12, Q13, Q14, Q15, Q16, Q17, Q18, Q19, Q20, Q21, Q22]), "oppositeDirection" : true, "depth" : 1.52 * mm, "offsetDistance" : 25.4 * mm});
        }
        {
            var Q0;
            Q0 = qSketchRegion(id + "F3", true);
            extrude(context, id + "F10", {"entities" : qUnion([Q0]), "operationType" : NewBodyOperationType.ADD, "depth" : 0.25 * mm, "offsetDistance" : 25.4 * mm});
        }
        {
            var Q0;
            Q0 = qSketchRegion(id + "F4", true);
            extrude(context, id + "F11", {"entities" : qUnion([Q0]), "operationType" : NewBodyOperationType.ADD, "depth" : 0.5 * mm, "offsetDistance" : 25.4 * mm});
        }
        {
            var Q0;
            {var subQ2=sQuery(id+"F0.wireOp",EDGE,"E4");Q0=makeQuery(id+"F0.imprint","IMPRINT",FACE,{"disambiguationData":[TD([[makeQuery(id+"F0.imprint","IMPRINT",EDGE,{"derivedFrom":subQ2}),-1.0]])]});}
            var sketch = newSketch(context, id + "F12", { "sketchPlane" : qUnion([Q0])});
            skFitSpline(sketch, "E158", {"points": [v(17.45, 27.47) * mm, v(18.4, 27.1) * mm, v(19.1, 26.42) * mm, v(19.78, 25.3) * mm, v(20.19, 24.22) * mm, v(20.42, 23.52) * mm, v(20.8, 21.94) * mm, v(20.9, 20.78) * mm, v(20.9, 19.13) * mm, v(20.66, 18.25) * mm, v(20.24, 17.49) * mm, v(19.6, 17) * mm, v(18.92, 16.72) * mm, v(17.56, 16.58) * mm, v(16.71, 16.8) * mm, v(16.02, 17.44) * mm, v(15.61, 18.1) * mm, v(15.46, 19.02) * mm, v(15.51, 19.99) * mm, v(15.75, 20.87) * mm, v(15.76, 20.86) * mm], "startDerivative": vector(19.47, -5.45) * mm, "endDerivative": vector(0.67, -3.02) * mm});
            skLineSegment(sketch, "E159", {"start": v(15.75, 20.87) * mm, "end": v(16.25, 21.2) * mm});
            skLineSegment(sketch, "E160", {"start": v(16.25, 21.2) * mm, "end": v(16.88, 21.83) * mm});
            skLineSegment(sketch, "E161", {"start": v(16.88, 21.83) * mm, "end": v(17.39, 22.59) * mm});
            skLineSegment(sketch, "E162", {"start": v(17.39, 22.59) * mm, "end": v(17.7, 23.46) * mm});
            skLineSegment(sketch, "E163", {"start": v(17.7, 23.46) * mm, "end": v(17.77, 24.8) * mm});
            skLineSegment(sketch, "E164", {"start": v(17.77, 24.8) * mm, "end": v(17.55, 25.67) * mm});
            skLineSegment(sketch, "E165", {"start": v(17.55, 25.67) * mm, "end": v(17.1, 26.5) * mm});
            skLineSegment(sketch, "E166", {"start": v(17.1, 26.5) * mm, "end": v(16.6, 27.03) * mm});
            skLineSegment(sketch, "E167", {"start": v(16.6, 27.03) * mm, "end": v(16.26, 27.34) * mm});
            skFitSpline(sketch, "E168", {"points": [v(17.45, 27.47) * mm, v(16.87, 27.55) * mm, v(16.26, 27.34) * mm], "startDerivative": vector(-1.18, 0.3) * mm, "endDerivative": vector(-1.19, -0.55) * mm});
            skSolve(sketch);
        }
        {
            var Q0;
            Q0 = qSketchRegion(id + "F12", true);
            extrude(context, id + "F13", {"entities" : qUnion([Q0]), "operationType" : NewBodyOperationType.ADD, "depth" : 0.1 * mm, "offsetDistance" : 25.4 * mm});
        }
        {
            var Q0;
            {var subQ2=sQuery(id+"F0.wireOp",EDGE,"E4");Q0=makeQuery(id+"F0.imprint","IMPRINT",FACE,{"disambiguationData":[TD([[makeQuery(id+"F0.imprint","IMPRINT",EDGE,{"derivedFrom":subQ2}),-1.0]])]});}
            var sketch = newSketch(context, id + "F14", { "sketchPlane" : qUnion([Q0])});
            skArc(sketch, "E169", {"start": v(14.64, 27.27) * mm, "mid": v(14.42, 27.28) * mm, "end": v(14.19, 27.28) * mm});
            skPoint(sketch, "E169.first.point", {"position": v(14.19, 27.28) * mm});
            skPoint(sketch, "E169.second.point", {"position": v(14.78, 20.7) * mm});
            skPoint(sketch, "E169.third.point", {"position": v(12.27, 21.43) * mm});
            skFitSpline(sketch, "E170", {"points": [v(17.68, 23.73) * mm, v(17.72, 24.86) * mm, v(17.34, 26.06) * mm, v(16.3, 27.32) * mm, v(16.33, 27.33) * mm, v(16.33, 27.35) * mm], "startDerivative": vector(0.27, 4.09) * mm, "endDerivative": vector(-0.2, 0.67) * mm});
            skLineSegment(sketch, "E171", {"start": v(14.64, 27.27) * mm, "end": v(16.16, 27.32) * mm});
            skLineSegment(sketch, "E172", {"start": v(16.82, 26.8) * mm, "end": v(17.34, 26.06) * mm});
            skLineSegment(sketch, "E173", {"start": v(17.34, 26.06) * mm, "end": v(17.72, 24.86) * mm});
            skLineSegment(sketch, "E174", {"start": v(17.72, 24.86) * mm, "end": v(17.7, 24.11) * mm});
            skLineSegment(sketch, "E175", {"start": v(17.7, 24.11) * mm, "end": v(17.68, 23.78) * mm});
            skFitSpline(sketch, "E176", {"points": [v(16.16, 27.32) * mm, v(16.82, 26.8) * mm], "startDerivative": vector(0.66, -0.52) * mm, "endDerivative": vector(0.66, -0.52) * mm});
            skLineSegment(sketch, "E177", {"start": v(12.68, 27.32) * mm, "end": v(14.19, 27.28) * mm});
            skArc(sketch, "E178.trimOffspring", {"start": v(11.22, 24.95) * mm, "mid": v(13.8, 20.72) * mm, "end": v(17.68, 23.78) * mm});
            skFitSpline(sketch, "E179", {"points": [v(11.22, 24.95) * mm, v(11.5, 25.93) * mm, v(12.68, 27.32) * mm], "startDerivative": vector(0.35, 2.26) * mm, "endDerivative": vector(2.47, 2.46) * mm});
            skSolve(sketch);
        }
        {
            var Q0;
            {var subQ1=sQuery(id+"F14.wireOp",EDGE,"E169");Q0=makeQuery(id+"F14.imprint","IMPRINT",FACE,{"disambiguationData":[TD([[makeQuery(id+"F14.imprint","IMPRINT",EDGE,{"derivedFrom":subQ1}),1.0]])]});}
            extrude(context, id + "F15", {"entities" : qUnion([Q0]), "operationType" : NewBodyOperationType.REMOVE, "oppositeDirection" : true, "depth" : 2.54 * mm, "offsetDistance" : 25.4 * mm});
        }
        {
            var Q0;
            Q0=makeQuery(id+"F6.opExtrude","CAP_FACE",FACE,{"disambiguationData":[OSD([sQuery(id+"F0.wireOp",EDGE,"E0"),sQuery(id+"F0.wireOp",EDGE,"E1"),sQuery(id+"F0.wireOp",EDGE,"E25"),sQuery(id+"F0.wireOp",EDGE,"E28"),sQuery(id+"F0.wireOp",EDGE,"E65"),sQuery(id+"F0.wireOp",EDGE,"E89")])],"isStart":false});
            cPlane(context, id + "F16", {"entities" : qUnion([Q0]), "cplaneType" : CPlaneType.OFFSET, "offset" : 25.4 * mm, "width" : 152.4 * mm, "height" : 152.4 * mm});
        }
        {
            var Q0;
            Q0=qCreatedBy(id+"F16.planeOp",FACE);
            var sketch = newSketch(context, id + "F17", { "sketchPlane" : qUnion([Q0])});
            skFitSpline(sketch, "E180.0", {"points": [v(22.3, -27.84) * mm, v(22.19, -26.86) * mm, v(21.98, -25.08) * mm, v(21.81, -23.2) * mm, v(21.73, -21.6) * mm, v(22.93, -18.81) * mm, v(23.73, -17.05) * mm, v(24.56, -15.05) * mm, v(25.02, -13.17) * mm, v(25.17, -11.52) * mm, v(25.06, -9.82) * mm, v(24.9, -8.46) * mm, v(23.55, -5.7) * mm, v(22.33, -4.6) * mm, v(20.82, -3.47) * mm, v(19.22, -3.02) * mm, v(17.28, -2.53) * mm, v(15.27, -2.31) * mm, v(13.18, -2.11) * mm, v(8.93, -1.84) * mm, v(6.91, -2.79) * mm, v(4.9, -3.85) * mm, v(3.8, -5.78) * mm, v(2.97, -7.78) * mm, v(2.96, -9.91) * mm, v(3.17, -12.9) * mm, v(4.54, -16.04) * mm, v(5.63, -18.29) * mm, v(6.62, -21.11) * mm, v(6.82, -23.32) * mm, v(6.18, -26.43) * mm, v(6, -28.59) * mm, v(6.31, -31.25) * mm, v(8.26, -33.1) * mm, v(10.39, -34.36) * mm, v(11.96, -34.48) * mm, v(12.74, -34.53) * mm]});
            skFitSpline(sketch, "E181.0", {"points": [v(22.3, -27.84) * mm, v(22.3, -28.19) * mm, v(22.3, -28.95) * mm, v(22.3, -30.48) * mm, v(21.66, -31.94) * mm, v(20.86, -32.93) * mm, v(19.34, -33.94) * mm, v(18.04, -34.4) * mm, v(16.55, -34.58) * mm, v(16.2, -34.55) * mm, v(16.07, -34.53) * mm]});
            skLineSegment(sketch, "E182.0", {"start": v(12.74, -34.53) * mm, "end": v(16.07, -34.53) * mm});
            skFitSpline(sketch, "E183.0", {"points": [v(16, -33) * mm, v(14.52, -33.08) * mm, v(10.92, -33.65) * mm, v(6.4, -30.07) * mm, v(9.14, -23.52) * mm, v(7.35, -17.6) * mm, v(5.3, -13.06) * mm, v(3.46, -7.8) * mm, v(9.02, -3.48) * mm, v(9.77, -3.97) * mm, v(15.85, -4.13) * mm, v(20.17, -4.25) * mm, v(24.7, -10.27) * mm, v(20.85, -18.83) * mm, v(18.85, -22.96) * mm, v(21.59, -28.5) * mm, v(19.17, -33.1) * mm, v(17.14, -32.95) * mm, v(16, -33) * mm]});
            skSolve(sketch);
        }
        {
            var Q0;
            Q0=makeQuery(id+"F17.imprint","IMPRINT",FACE,{"disambiguationData":[TD([[makeQuery(id+"F17.imprint","IMPRINT",EDGE,{"derivedFrom":sQuery(id+"F17.wireOp",EDGE,"E183.0")}),-1.0]])]});
            extrude(context, id + "F18", {"entities" : qUnion([Q0]), "depth" : 1.27 * mm, "offsetDistance" : 25.4 * mm});
        }
        {
            var Q0;
            Q0=makeQuery(id+"F18.opExtrude","SWEPT_BODY",BODY,{"disambiguationData":[OSD([sQuery(id+"F17.wireOp",EDGE,"E183.0")])]});
            transform(context, id + "F19", {"entities" : qUnion([Q0]), "transformType" : TransformType.TRANSLATION_3D, "dx" : 0 * mm, "dy" : 0 * mm, "dz" : 26.62 * mm, "makeCopy" : false});
        }
        {
            var Q0;
            Q0=makeQuery(id+"F0.imprint","IMPRINT",FACE,{"disambiguationData":[TD([[makeQuery(id+"F0.imprint","IMPRINT",EDGE,{"derivedFrom":sQuery(id+"F0.wireOp",EDGE,"E98")}),-1.0]])]});
            var Q1;
            {var subQ0=sQuery(id+"F0.wireOp",EDGE,"E122.MirrorCS");Q1=makeQuery(id+"F0.imprint","IMPRINT",FACE,{"disambiguationData":[TD([[makeQuery(id+"F0.imprint","IMPRINT",EDGE,{"derivedFrom":subQ0}),1.0]])]});}
            var Q2;
            Q2=makeQuery(id+"F0.imprint","IMPRINT",FACE,{"disambiguationData":[TD([[makeQuery(id+"F0.imprint","IMPRINT",EDGE,{"derivedFrom":sQuery(id+"F0.wireOp",EDGE,"E105")}),1.0]])]});
            var Q3;
            {var subQ0=sQuery(id+"F0.wireOp",EDGE,"E124.MirrorCS");Q3=makeQuery(id+"F0.imprint","IMPRINT",FACE,{"disambiguationData":[TD([[makeQuery(id+"F0.imprint","IMPRINT",EDGE,{"derivedFrom":subQ0}),-1.0]])]});}
            var Q4;
            Q4=makeQuery(id+"F0.imprint","IMPRINT",FACE,{"disambiguationData":[TD([[makeQuery(id+"F0.imprint","IMPRINT",EDGE,{"derivedFrom":sQuery(id+"F0.wireOp",EDGE,"E104")}),1.0]])]});
            var Q5;
            {var subQ0=sQuery(id+"F0.wireOp",EDGE,"E128.MirrorCS");Q5=makeQuery(id+"F0.imprint","IMPRINT",FACE,{"disambiguationData":[TD([[makeQuery(id+"F0.imprint","IMPRINT",EDGE,{"derivedFrom":subQ0}),-1.0]])]});}
            extrude(context, id + "F20", {"entities" : qUnion([Q0, Q1, Q2, Q3, Q4, Q5]), "operationType" : NewBodyOperationType.ADD, "oppositeDirection" : true, "depth" : 0.25 * mm, "offsetDistance" : 25.4 * mm});
        }
        {
            var Q0;
            Q0=makeQuery(id+"F2.opExtrude","CAP_FACE",FACE,{"disambiguationData":[OSD([sQuery(id+"F0.wireOp",EDGE,"E2"),sQuery(id+"F0.wireOp",EDGE,"E90"),sQuery(id+"F0.wireOp",EDGE,"E91"),sQuery(id+"F0.wireOp",EDGE,"E92"),sQuery(id+"F0.wireOp",EDGE,"E93"),sQuery(id+"F0.wireOp",EDGE,"E95"),sQuery(id+"F0.wireOp",EDGE,"E97.bottom"),sQuery(id+"F0.wireOp",EDGE,"E97.top"),sQuery(id+"F0.wireOp",EDGE,"E97.left"),sQuery(id+"F0.wireOp",EDGE,"E97.right"),sQuery(id+"F0.wireOp",EDGE,"E99"),sQuery(id+"F0.wireOp",EDGE,"E101"),sQuery(id+"F0.wireOp",EDGE,"E106"),sQuery(id+"F0.wireOp",EDGE,"E108"),sQuery(id+"F0.wireOp",EDGE,"E109.trimOffspring"),sQuery(id+"F0.wireOp",EDGE,"E110"),sQuery(id+"F0.wireOp",EDGE,"E112"),sQuery(id+"F0.wireOp",EDGE,"E114"),sQuery(id+"F0.wireOp",EDGE,"E115.MirrorCS"),sQuery(id+"F0.wireOp",EDGE,"E116.MirrorCS"),sQuery(id+"F0.wireOp",EDGE,"E117.MirrorCS"),sQuery(id+"F0.wireOp",EDGE,"E118.MirrorCS"),sQuery(id+"F0.wireOp",EDGE,"E119.MirrorCS"),sQuery(id+"F0.wireOp",EDGE,"E121.MirrorCS"),sQuery(id+"F0.wireOp",EDGE,"E126.MirrorCS"),sQuery(id+"F0.wireOp",EDGE,"E127.MirrorCS"),sQuery(id+"F0.wireOp",EDGE,"E120.MirrorCS"),sQuery(id+"F0.wireOp",EDGE,"E132.MirrorCS"),sQuery(id+"F0.wireOp",EDGE,"E133.MirrorCS")])],"isStart":false});
            var sketch = newSketch(context, id + "F21", { "sketchPlane" : qUnion([Q0])});
            skLineSegment(sketch, "E184", {"start": v(16, 61.5) * mm, "end": v(16.41, 61.5) * mm});
            skLineSegment(sketch, "E185", {"start": v(16.41, 61.5) * mm, "end": v(16.41, 61.26) * mm});
            skLineSegment(sketch, "E186", {"start": v(16.41, 61.26) * mm, "end": v(16, 61.26) * mm});
            skLineSegment(sketch, "E187", {"start": v(16, 59.08) * mm, "end": v(16.42, 59.08) * mm});
            skLineSegment(sketch, "E188", {"start": v(16.42, 59.08) * mm, "end": v(16.42, 58.85) * mm});
            skLineSegment(sketch, "E189", {"start": v(16.42, 58.85) * mm, "end": v(16, 58.85) * mm});
            skLineSegment(sketch, "E190", {"start": v(16, 56.5) * mm, "end": v(16.42, 56.5) * mm});
            skLineSegment(sketch, "E191", {"start": v(16.42, 56.5) * mm, "end": v(16.42, 56.25) * mm});
            skLineSegment(sketch, "E192", {"start": v(16.42, 56.25) * mm, "end": v(16, 56.25) * mm});
            skLineSegment(sketch, "E193", {"start": v(14.27, 63.18) * mm, "end": v(14.33, 54.52) * mm, "construction": true});
            skLineSegment(sketch, "E194.MirrorCS", {"start": v(12.15, 61.22) * mm, "end": v(12.53, 61.23) * mm});
            skLineSegment(sketch, "E195.MirrorCS", {"start": v(12.53, 61.47) * mm, "end": v(12.14, 61.47) * mm});
            skLineSegment(sketch, "E196.MirrorCS", {"start": v(12.14, 61.47) * mm, "end": v(12.15, 61.22) * mm});
            skLineSegment(sketch, "E197.MirrorCS", {"start": v(12.53, 59.05) * mm, "end": v(12.18, 59.04) * mm});
            skLineSegment(sketch, "E198.MirrorCS", {"start": v(12.18, 59.04) * mm, "end": v(12.18, 58.81) * mm});
            skLineSegment(sketch, "E199.MirrorCS", {"start": v(12.18, 58.81) * mm, "end": v(12.53, 58.82) * mm});
            skLineSegment(sketch, "E200.MirrorCS", {"start": v(12.53, 56.47) * mm, "end": v(12.21, 56.47) * mm});
            skLineSegment(sketch, "E201.MirrorCS", {"start": v(12.22, 56.22) * mm, "end": v(12.53, 56.23) * mm});
            skLineSegment(sketch, "E202.MirrorCS", {"start": v(12.21, 56.47) * mm, "end": v(12.22, 56.22) * mm});
            skLineSegment(sketch, "E203", {"start": v(16.41, 61.5) * mm, "end": v(16.41, 61.63) * mm});
            skLineSegment(sketch, "E204", {"start": v(16.41, 61.63) * mm, "end": v(16.6, 61.63) * mm});
            skLineSegment(sketch, "E205", {"start": v(16.6, 61.63) * mm, "end": v(16.74, 61.5) * mm});
            skPoint(sketch, "E206.end.orphan", {"position": v(16.41, 61.2) * mm});
            skLineSegment(sketch, "E207", {"start": v(16.74, 61.5) * mm, "end": v(16.74, 61.25) * mm});
            skLineSegment(sketch, "E208", {"start": v(16.74, 61.25) * mm, "end": v(16.6, 61.12) * mm});
            skLineSegment(sketch, "E209", {"start": v(16.6, 61.12) * mm, "end": v(16.41, 61.12) * mm});
            skLineSegment(sketch, "E210", {"start": v(16.41, 61.12) * mm, "end": v(16.41, 61.26) * mm});
            skLineSegment(sketch, "E211.MirrorCS", {"start": v(12.14, 61.6) * mm, "end": v(11.95, 61.6) * mm});
            skLineSegment(sketch, "E212.MirrorCS", {"start": v(11.81, 61.46) * mm, "end": v(11.82, 61.22) * mm});
            skLineSegment(sketch, "E213.MirrorCS", {"start": v(11.95, 61.6) * mm, "end": v(11.81, 61.46) * mm});
            skLineSegment(sketch, "E214.MirrorCS", {"start": v(12.14, 61.47) * mm, "end": v(12.14, 61.6) * mm});
            skLineSegment(sketch, "E215.MirrorCS", {"start": v(11.97, 61.09) * mm, "end": v(12.15, 61.09) * mm});
            skLineSegment(sketch, "E216.MirrorCS", {"start": v(11.82, 61.22) * mm, "end": v(11.97, 61.09) * mm});
            skLineSegment(sketch, "E217.MirrorCS", {"start": v(12.15, 61.09) * mm, "end": v(12.15, 61.22) * mm});
            skLineSegment(sketch, "E218", {"start": v(16.42, 59.08) * mm, "end": v(16.42, 59.2) * mm});
            skLineSegment(sketch, "E219", {"start": v(16.42, 59.2) * mm, "end": v(16.58, 59.2) * mm});
            skLineSegment(sketch, "E220", {"start": v(16.58, 59.2) * mm, "end": v(16.7, 59.08) * mm});
            skLineSegment(sketch, "E221", {"start": v(16.7, 59.08) * mm, "end": v(16.7, 58.84) * mm});
            skLineSegment(sketch, "E222", {"start": v(16.42, 58.76) * mm, "end": v(16.42, 58.85) * mm});
            skLineSegment(sketch, "E223", {"start": v(16.7, 58.84) * mm, "end": v(16.6, 58.71) * mm});
            skLineSegment(sketch, "E224", {"start": v(16.6, 58.71) * mm, "end": v(16.42, 58.71) * mm});
            skLineSegment(sketch, "E225", {"start": v(16.42, 58.71) * mm, "end": v(16.42, 58.76) * mm});
            skLineSegment(sketch, "E226", {"start": v(16.42, 56.5) * mm, "end": v(16.42, 56.63) * mm});
            skLineSegment(sketch, "E227", {"start": v(16.42, 56.63) * mm, "end": v(16.55, 56.63) * mm});
            skLineSegment(sketch, "E228", {"start": v(16.55, 56.63) * mm, "end": v(16.7, 56.5) * mm});
            skLineSegment(sketch, "E229", {"start": v(16.7, 56.5) * mm, "end": v(16.7, 56.25) * mm});
            skLineSegment(sketch, "E230", {"start": v(16.7, 56.25) * mm, "end": v(16.57, 56.15) * mm});
            skLineSegment(sketch, "E231", {"start": v(16.57, 56.15) * mm, "end": v(16.42, 56.14) * mm});
            skLineSegment(sketch, "E232", {"start": v(16.42, 56.14) * mm, "end": v(16.42, 56.25) * mm});
            skLineSegment(sketch, "E233.MirrorCS", {"start": v(12.17, 59.17) * mm, "end": v(12, 59.16) * mm});
            skLineSegment(sketch, "E234.MirrorCS", {"start": v(12.18, 59.04) * mm, "end": v(12.17, 59.17) * mm});
            skLineSegment(sketch, "E235.MirrorCS", {"start": v(12, 58.68) * mm, "end": v(12.18, 58.68) * mm});
            skLineSegment(sketch, "E236.MirrorCS", {"start": v(12.18, 58.72) * mm, "end": v(12.18, 58.81) * mm});
            skLineSegment(sketch, "E237.MirrorCS", {"start": v(12.18, 58.68) * mm, "end": v(12.18, 58.72) * mm});
            skLineSegment(sketch, "E238.MirrorCS", {"start": v(11.9, 58.8) * mm, "end": v(12, 58.68) * mm});
            skLineSegment(sketch, "E239.MirrorCS", {"start": v(11.9, 59.04) * mm, "end": v(11.9, 58.8) * mm});
            skLineSegment(sketch, "E240.MirrorCS", {"start": v(12, 59.16) * mm, "end": v(11.9, 59.04) * mm});
            skLineSegment(sketch, "E241.MirrorCS", {"start": v(12.08, 56.6) * mm, "end": v(11.93, 56.46) * mm});
            skLineSegment(sketch, "E242.MirrorCS", {"start": v(11.93, 56.46) * mm, "end": v(11.93, 56.22) * mm});
            skLineSegment(sketch, "E243.MirrorCS", {"start": v(11.93, 56.22) * mm, "end": v(12.07, 56.11) * mm});
            skLineSegment(sketch, "E244.MirrorCS", {"start": v(12.07, 56.11) * mm, "end": v(12.22, 56.11) * mm});
            skLineSegment(sketch, "E245.MirrorCS", {"start": v(12.22, 56.11) * mm, "end": v(12.22, 56.22) * mm});
            skLineSegment(sketch, "E246.MirrorCS", {"start": v(12.21, 56.47) * mm, "end": v(12.21, 56.6) * mm});
            skLineSegment(sketch, "E247.MirrorCS", {"start": v(12.21, 56.6) * mm, "end": v(12.08, 56.6) * mm});
            skPoint(sketch, "E248.orphan", {"position": v(12.63, 56.47) * mm});
            skPoint(sketch, "E249.orphan", {"position": v(12.63, 56.23) * mm});
            skPoint(sketch, "E250.startSnap0", {"position": v(12.53, 58.84) * mm});
            skPoint(sketch, "E251.orphan", {"position": v(12.56, 61.47) * mm});
            skPoint(sketch, "E252.orphan", {"position": v(12.56, 61.23) * mm});
            skPoint(sketch, "E253.start.orphan", {"position": v(12.5, 61.22) * mm});
            skPoint(sketch, "E254.orphan", {"position": v(12.6, 58.82) * mm});
            skPoint(sketch, "E255.orphan", {"position": v(12.6, 59.05) * mm});
            skPoint(sketch, "E250.end.orphan", {"position": v(12.5, 58.75) * mm});
            skPoint(sketch, "E256.end.orphan", {"position": v(12.5, 59.15) * mm});
            skSolve(sketch);
        }
        {
            var Q0;
            {var subQ0=sQuery(id+"F21.wireOp",EDGE,"E194.MirrorCS");Q0=makeQuery(id+"F21.imprint","IMPRINT",FACE,{"disambiguationData":[TD([[makeQuery(id+"F21.imprint","IMPRINT",EDGE,{"derivedFrom":subQ0}),1.0]])]});}
            var Q1;
            Q1=makeQuery(id+"F21.imprint","IMPRINT",FACE,{"disambiguationData":[TD([[makeQuery(id+"F21.imprint","IMPRINT",EDGE,{"derivedFrom":sQuery(id+"F21.wireOp",EDGE,"E196.MirrorCS")}),-1.0]])]});
            var Q2;
            {var subQ0=sQuery(id+"F21.wireOp",EDGE,"E197.MirrorCS");Q2=makeQuery(id+"F21.imprint","IMPRINT",FACE,{"disambiguationData":[TD([[makeQuery(id+"F21.imprint","IMPRINT",EDGE,{"derivedFrom":subQ0}),1.0]])]});}
            var Q3;
            Q3=makeQuery(id+"F21.imprint","IMPRINT",FACE,{"disambiguationData":[TD([[makeQuery(id+"F21.imprint","IMPRINT",EDGE,{"derivedFrom":sQuery(id+"F21.wireOp",EDGE,"E198.MirrorCS")}),-1.0]])]});
            var Q4;
            {var subQ0=sQuery(id+"F21.wireOp",EDGE,"E200.MirrorCS");Q4=makeQuery(id+"F21.imprint","IMPRINT",FACE,{"disambiguationData":[TD([[makeQuery(id+"F21.imprint","IMPRINT",EDGE,{"derivedFrom":subQ0}),1.0]])]});}
            var Q5;
            Q5=makeQuery(id+"F21.imprint","IMPRINT",FACE,{"disambiguationData":[TD([[makeQuery(id+"F21.imprint","IMPRINT",EDGE,{"derivedFrom":sQuery(id+"F21.wireOp",EDGE,"E241.MirrorCS")}),1.0]])]});
            var Q6;
            Q6=makeQuery(id+"F21.imprint","IMPRINT",FACE,{"disambiguationData":[TD([[makeQuery(id+"F21.imprint","IMPRINT",EDGE,{"derivedFrom":sQuery(id+"F21.wireOp",EDGE,"E191")}),1.0]])]});
            var Q7;
            Q7=makeQuery(id+"F21.imprint","IMPRINT",FACE,{"disambiguationData":[TD([[makeQuery(id+"F21.imprint","IMPRINT",EDGE,{"derivedFrom":sQuery(id+"F21.wireOp",EDGE,"E188")}),1.0]])]});
            var Q8;
            Q8=makeQuery(id+"F21.imprint","IMPRINT",FACE,{"disambiguationData":[TD([[makeQuery(id+"F21.imprint","IMPRINT",EDGE,{"derivedFrom":sQuery(id+"F21.wireOp",EDGE,"E185")}),1.0]])]});
            var Q9;
            {var subQ0=sQuery(id+"F21.wireOp",EDGE,"E184");Q9=makeQuery(id+"F21.imprint","IMPRINT",FACE,{"disambiguationData":[TD([[makeQuery(id+"F21.imprint","IMPRINT",EDGE,{"derivedFrom":subQ0}),-1.0]])]});}
            var Q10;
            {var subQ0=sQuery(id+"F21.wireOp",EDGE,"E187");Q10=makeQuery(id+"F21.imprint","IMPRINT",FACE,{"disambiguationData":[TD([[makeQuery(id+"F21.imprint","IMPRINT",EDGE,{"derivedFrom":subQ0}),-1.0]])]});}
            var Q11;
            {var subQ0=sQuery(id+"F21.wireOp",EDGE,"E190");Q11=makeQuery(id+"F21.imprint","IMPRINT",FACE,{"disambiguationData":[TD([[makeQuery(id+"F21.imprint","IMPRINT",EDGE,{"derivedFrom":subQ0}),-1.0]])]});}
            extrude(context, id + "F22", {"entities" : qUnion([Q0, Q1, Q2, Q3, Q4, Q5, Q6, Q7, Q8, Q9, Q10, Q11]), "operationType" : NewBodyOperationType.ADD, "oppositeDirection" : true, "depth" : 0.2 * mm, "offsetDistance" : 25.4 * mm});
        }
    });
